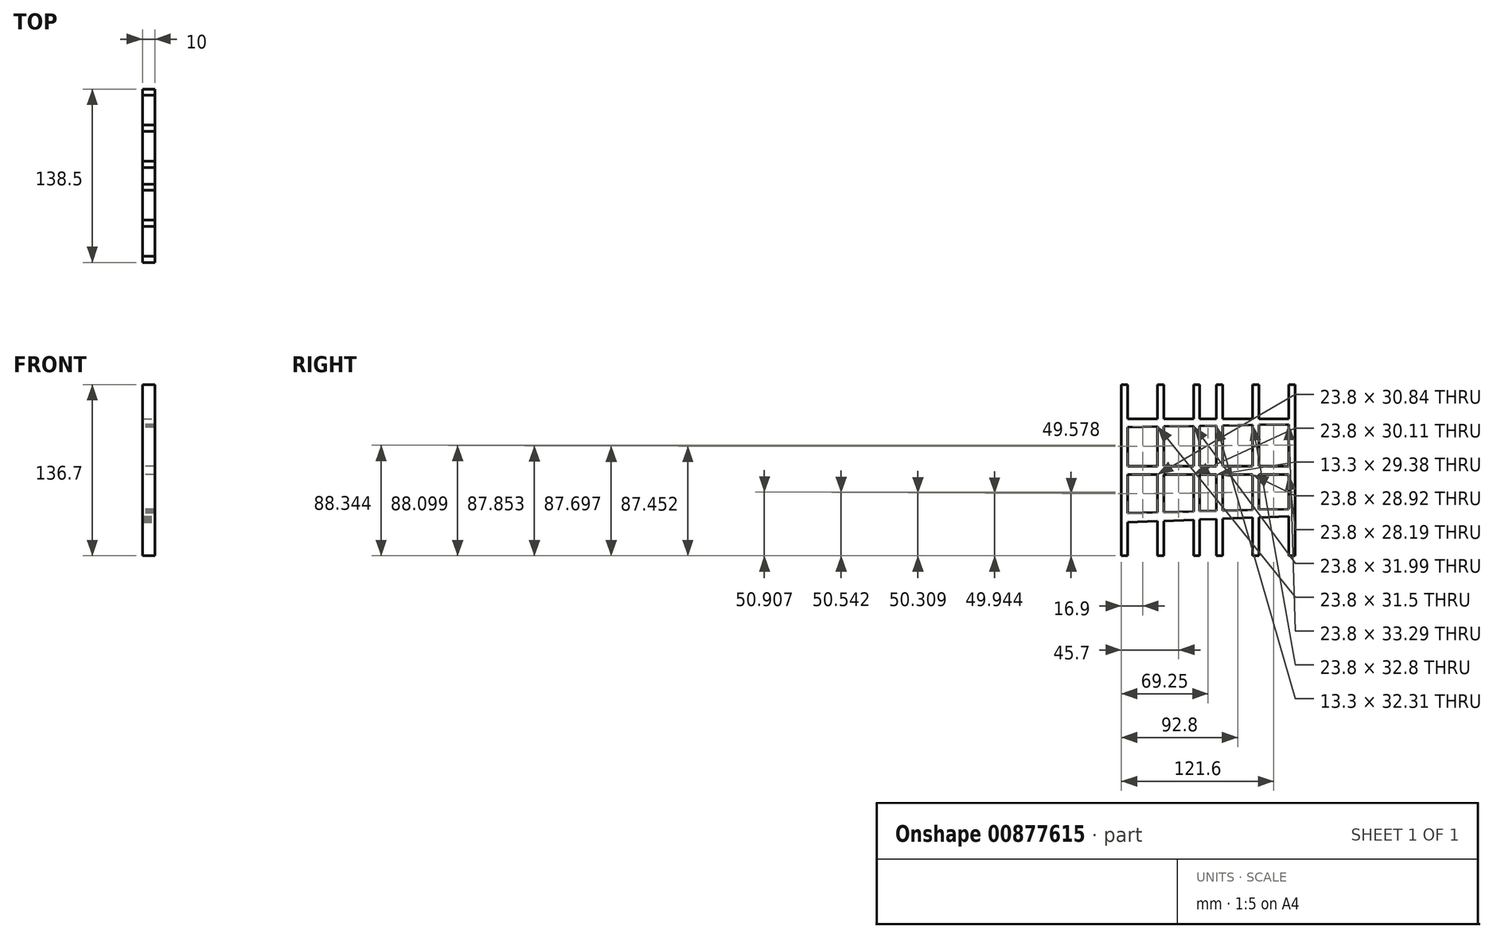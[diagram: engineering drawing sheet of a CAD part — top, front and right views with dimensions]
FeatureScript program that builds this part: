
annotation { "Feature Type Name" : "Feature", "Feature Type Description" : "" }
export const myFeature = defineFeature(function(context is Context, id is Id, definition is map)
    precondition{}
    {
        {
            var Q0;
            Q0=qCreatedBy(makeId("Right.planeOp"),FACE);
            var sketch = newSketch(context, id + "F0", { "sketchPlane" : qUnion([Q0])});
            skLineSegment(sketch, "E0", {"start": v(0, 0) * mm, "end": v(0, -65) * mm});
            skLineSegment(sketch, "E1", {"start": v(0, 0) * mm, "end": v(0, 65) * mm});
            skLineSegment(sketch, "E2", {"start": v(0, 0) * mm, "end": v(-5, 0) * mm});
            skLineSegment(sketch, "E3", {"start": v(-5, 0) * mm, "end": v(-5, 65) * mm});
            skLineSegment(sketch, "E4", {"start": v(-5, 65) * mm, "end": v(0, 65) * mm});
            skLineSegment(sketch, "E5", {"start": v(-5, 0) * mm, "end": v(-5, -65) * mm});
            skLineSegment(sketch, "E6", {"start": v(-5, -65) * mm, "end": v(0, -65) * mm});
            skLineSegment(sketch, "E7.0.1.0", {"start": v(-5, -6.7) * mm, "end": v(-5, 58.3) * mm});
            skLineSegment(sketch, "E7.0.1.1", {"start": v(0, -6.7) * mm, "end": v(0, -71.7) * mm});
            skLineSegment(sketch, "E7.0.1.2", {"start": v(0, -6.7) * mm, "end": v(0, 58.3) * mm});
            skLineSegment(sketch, "E7.0.1.3", {"start": v(-5, -6.7) * mm, "end": v(-5, -71.7) * mm});
            skLineSegment(sketch, "E7.0.1.4", {"start": v(-5, 58.3) * mm, "end": v(0, 58.3) * mm});
            skLineSegment(sketch, "E7.0.1.5", {"start": v(-5, -71.7) * mm, "end": v(0, -71.7) * mm});
            skLineSegment(sketch, "E7.0.1.6", {"start": v(0, -6.7) * mm, "end": v(-5, -6.7) * mm});
            skLineSegment(sketch, "E7.1.0.0", {"start": v(-33.8, 0) * mm, "end": v(-33.8, 65) * mm});
            skLineSegment(sketch, "E7.1.0.1", {"start": v(-28.8, 0) * mm, "end": v(-28.8, -65) * mm});
            skLineSegment(sketch, "E7.1.0.2", {"start": v(-28.8, 0) * mm, "end": v(-28.8, 65) * mm});
            skLineSegment(sketch, "E7.1.0.3", {"start": v(-33.8, 0) * mm, "end": v(-33.8, -65) * mm});
            skLineSegment(sketch, "E7.1.0.4", {"start": v(-33.8, 65) * mm, "end": v(-28.8, 65) * mm});
            skLineSegment(sketch, "E7.1.0.5", {"start": v(-33.8, -65) * mm, "end": v(-28.8, -65) * mm});
            skLineSegment(sketch, "E7.1.0.6", {"start": v(-28.8, 0) * mm, "end": v(-33.8, 0) * mm});
            skLineSegment(sketch, "E7.1.1.0", {"start": v(-33.8, -6.7) * mm, "end": v(-33.8, 58.3) * mm});
            skLineSegment(sketch, "E7.1.1.1", {"start": v(-28.8, -6.7) * mm, "end": v(-28.8, -71.7) * mm});
            skLineSegment(sketch, "E7.1.1.2", {"start": v(-28.8, -6.7) * mm, "end": v(-28.8, 58.3) * mm});
            skLineSegment(sketch, "E7.1.1.3", {"start": v(-33.8, -6.7) * mm, "end": v(-33.8, -71.7) * mm});
            skLineSegment(sketch, "E7.1.1.4", {"start": v(-33.8, 58.3) * mm, "end": v(-28.8, 58.3) * mm});
            skLineSegment(sketch, "E7.1.1.5", {"start": v(-33.8, -71.7) * mm, "end": v(-28.8, -71.7) * mm});
            skLineSegment(sketch, "E7.1.1.6", {"start": v(-28.8, -6.7) * mm, "end": v(-33.8, -6.7) * mm});
            skLineSegment(sketch, "E7.2.0.0", {"start": v(-62.6, 0) * mm, "end": v(-62.6, 65) * mm});
            skLineSegment(sketch, "E7.2.0.1", {"start": v(-57.6, 0) * mm, "end": v(-57.6, -65) * mm});
            skLineSegment(sketch, "E7.2.0.2", {"start": v(-57.6, 0) * mm, "end": v(-57.6, 65) * mm});
            skLineSegment(sketch, "E7.2.0.3", {"start": v(-62.6, 0) * mm, "end": v(-62.6, -65) * mm});
            skLineSegment(sketch, "E7.2.0.4", {"start": v(-62.6, 65) * mm, "end": v(-57.6, 65) * mm});
            skLineSegment(sketch, "E7.2.0.5", {"start": v(-62.6, -65) * mm, "end": v(-57.6, -65) * mm});
            skLineSegment(sketch, "E7.2.0.6", {"start": v(-57.6, 0) * mm, "end": v(-62.6, 0) * mm});
            skLineSegment(sketch, "E7.2.1.0", {"start": v(-62.6, -6.7) * mm, "end": v(-62.6, 58.3) * mm});
            skLineSegment(sketch, "E7.2.1.1", {"start": v(-57.6, -6.7) * mm, "end": v(-57.6, -71.7) * mm});
            skLineSegment(sketch, "E7.2.1.2", {"start": v(-57.6, -6.7) * mm, "end": v(-57.6, 58.3) * mm});
            skLineSegment(sketch, "E7.2.1.3", {"start": v(-62.6, -6.7) * mm, "end": v(-62.6, -71.7) * mm});
            skLineSegment(sketch, "E7.2.1.4", {"start": v(-62.6, 58.3) * mm, "end": v(-57.6, 58.3) * mm});
            skLineSegment(sketch, "E7.2.1.5", {"start": v(-62.6, -71.7) * mm, "end": v(-57.6, -71.7) * mm});
            skLineSegment(sketch, "E7.2.1.6", {"start": v(-57.6, -6.7) * mm, "end": v(-62.6, -6.7) * mm});
            skLineSegment(sketch, "E7.direction1", {"start": v(-5, -65) * mm, "end": v(-33.8, -65) * mm, "construction": true});
            skLineSegment(sketch, "E7.direction2", {"start": v(-5, -65) * mm, "end": v(-5, -71.7) * mm, "construction": true});
            skLineSegment(sketch, "E8.1.0.0", {"start": v(70.9, -65) * mm, "end": v(70.9, -71.7) * mm, "construction": true});
            skLineSegment(sketch, "E8.1.0.1", {"start": v(13.3, 0) * mm, "end": v(13.3, 65) * mm});
            skLineSegment(sketch, "E8.1.0.2", {"start": v(42.1, -6.7) * mm, "end": v(42.1, -71.7) * mm});
            skLineSegment(sketch, "E8.1.0.3", {"start": v(70.9, -65) * mm, "end": v(42.1, -65) * mm, "construction": true});
            skLineSegment(sketch, "E8.1.0.4", {"start": v(70.9, 0) * mm, "end": v(70.9, 65) * mm});
            skLineSegment(sketch, "E8.1.0.5", {"start": v(75.9, 0) * mm, "end": v(75.9, 65) * mm});
            skLineSegment(sketch, "E8.1.0.6", {"start": v(47.1, -6.7) * mm, "end": v(47.1, -71.7) * mm});
            skLineSegment(sketch, "E8.1.0.7", {"start": v(13.3, -6.7) * mm, "end": v(13.3, -71.7) * mm});
            skLineSegment(sketch, "E8.1.0.8", {"start": v(18.3, 0) * mm, "end": v(18.3, 65) * mm});
            skLineSegment(sketch, "E8.1.0.9", {"start": v(18.3, -6.7) * mm, "end": v(18.3, 58.3) * mm});
            skLineSegment(sketch, "E8.1.0.10", {"start": v(18.3, 0) * mm, "end": v(18.3, -65) * mm});
            skLineSegment(sketch, "E8.1.0.11", {"start": v(18.3, -6.7) * mm, "end": v(18.3, -71.7) * mm});
            skLineSegment(sketch, "E8.1.0.12", {"start": v(70.9, -6.7) * mm, "end": v(70.9, 58.3) * mm});
            skLineSegment(sketch, "E8.1.0.13", {"start": v(13.3, 0) * mm, "end": v(13.3, -65) * mm});
            skLineSegment(sketch, "E8.1.0.14", {"start": v(13.3, -6.7) * mm, "end": v(13.3, 58.3) * mm});
            skLineSegment(sketch, "E8.1.0.15", {"start": v(75.9, -6.7) * mm, "end": v(75.9, -71.7) * mm});
            skLineSegment(sketch, "E8.1.0.16", {"start": v(47.1, 0) * mm, "end": v(47.1, -65) * mm});
            skLineSegment(sketch, "E8.1.0.17", {"start": v(75.9, -6.7) * mm, "end": v(75.9, 58.3) * mm});
            skLineSegment(sketch, "E8.1.0.18", {"start": v(42.1, 0) * mm, "end": v(42.1, -65) * mm});
            skLineSegment(sketch, "E8.1.0.19", {"start": v(70.9, -6.7) * mm, "end": v(70.9, -71.7) * mm});
            skLineSegment(sketch, "E8.1.0.20", {"start": v(47.1, 0) * mm, "end": v(47.1, 65) * mm});
            skLineSegment(sketch, "E8.1.0.21", {"start": v(42.1, 0) * mm, "end": v(42.1, 65) * mm});
            skLineSegment(sketch, "E8.1.0.22", {"start": v(75.9, 0) * mm, "end": v(75.9, -65) * mm});
            skLineSegment(sketch, "E8.1.0.23", {"start": v(47.1, -6.7) * mm, "end": v(47.1, 58.3) * mm});
            skLineSegment(sketch, "E8.1.0.24", {"start": v(70.9, 0) * mm, "end": v(70.9, -65) * mm});
            skLineSegment(sketch, "E8.1.0.25", {"start": v(42.1, -6.7) * mm, "end": v(42.1, 58.3) * mm});
            skLineSegment(sketch, "E8.1.0.26", {"start": v(13.3, -71.7) * mm, "end": v(18.3, -71.7) * mm});
            skLineSegment(sketch, "E8.1.0.27", {"start": v(42.1, -71.7) * mm, "end": v(47.1, -71.7) * mm});
            skLineSegment(sketch, "E8.1.0.28", {"start": v(42.1, 58.3) * mm, "end": v(47.1, 58.3) * mm});
            skLineSegment(sketch, "E8.1.0.29", {"start": v(70.9, 65) * mm, "end": v(75.9, 65) * mm});
            skLineSegment(sketch, "E8.1.0.30", {"start": v(13.3, 58.3) * mm, "end": v(18.3, 58.3) * mm});
            skLineSegment(sketch, "E8.1.0.31", {"start": v(70.9, -65) * mm, "end": v(75.9, -65) * mm});
            skLineSegment(sketch, "E8.1.0.32", {"start": v(42.1, -65) * mm, "end": v(47.1, -65) * mm});
            skLineSegment(sketch, "E8.1.0.33", {"start": v(42.1, 65) * mm, "end": v(47.1, 65) * mm});
            skLineSegment(sketch, "E8.1.0.34", {"start": v(13.3, -65) * mm, "end": v(18.3, -65) * mm});
            skLineSegment(sketch, "E8.1.0.35", {"start": v(13.3, 65) * mm, "end": v(18.3, 65) * mm});
            skLineSegment(sketch, "E8.1.0.36", {"start": v(70.9, 58.3) * mm, "end": v(75.9, 58.3) * mm});
            skLineSegment(sketch, "E8.1.0.37", {"start": v(70.9, -71.7) * mm, "end": v(75.9, -71.7) * mm});
            skLineSegment(sketch, "E8.1.0.38", {"start": v(47.1, -6.7) * mm, "end": v(42.1, -6.7) * mm});
            skLineSegment(sketch, "E8.1.0.39", {"start": v(18.3, -6.7) * mm, "end": v(13.3, -6.7) * mm});
            skLineSegment(sketch, "E8.1.0.40", {"start": v(75.9, 0) * mm, "end": v(70.9, 0) * mm});
            skLineSegment(sketch, "E8.1.0.41", {"start": v(47.1, 0) * mm, "end": v(42.1, 0) * mm});
            skLineSegment(sketch, "E8.1.0.42", {"start": v(18.3, 0) * mm, "end": v(13.3, 0) * mm});
            skLineSegment(sketch, "E8.1.0.43", {"start": v(75.9, -6.7) * mm, "end": v(70.9, -6.7) * mm});
            skLineSegment(sketch, "E8.direction1", {"start": v(-62.6, -71.7) * mm, "end": v(13.3, -71.7) * mm, "construction": true});
            skLineSegment(sketch, "E9", {"start": v(75.9, 0) * mm, "end": v(-62.6, 0) * mm});
            skLineSegment(sketch, "E10", {"start": v(-62.6, -6.7) * mm, "end": v(75.9, -6.7) * mm});
            skSolve(sketch);
        }
        {
            var Q0;
            Q0 = qSketchRegion(id + "F0", true);
            extrude(context, id + "F1", {"entities" : qUnion([Q0]), "depth" : 10 * mm, "offsetDistance" : 25 * mm});
        }
        {
            var Q0;
            Q0=qCreatedBy(makeId("Right.planeOp"),FACE);
            var sketch = newSketch(context, id + "F2", { "sketchPlane" : qUnion([Q0])});
            skLineSegment(sketch, "E11", {"start": v(72.77, 37.6) * mm, "end": v(-59.16, 37.6) * mm});
            skLineSegment(sketch, "E12", {"start": v(-59.16, 37.6) * mm, "end": v(-59.16, 31.07) * mm});
            skLineSegment(sketch, "E13", {"start": v(-59.16, 31.07) * mm, "end": v(72.2, 33.31) * mm});
            skLineSegment(sketch, "E14", {"start": v(72.2, 33.31) * mm, "end": v(72.77, 37.6) * mm});
            skLineSegment(sketch, "E15", {"start": v(72.4, -34.24) * mm, "end": v(-59.91, -37.6) * mm});
            skLineSegment(sketch, "E16", {"start": v(-59.91, -37.6) * mm, "end": v(-59.72, -45.06) * mm});
            skLineSegment(sketch, "E17", {"start": v(-59.72, -45.06) * mm, "end": v(72.77, -40.03) * mm});
            skLineSegment(sketch, "E18", {"start": v(72.77, -40.03) * mm, "end": v(72.4, -34.24) * mm});
            skSolve(sketch);
        }
        {
            var Q0;
            Q0=makeQuery(id+"F2.imprint","IMPRINT",FACE,{"disambiguationData":[TD([[makeQuery(id+"F2.imprint","IMPRINT",EDGE,{"derivedFrom":sQuery(id+"F2.wireOp",EDGE,"E15")}),1.0]])]});
            var Q1;
            Q1=makeQuery(id+"F2.imprint","IMPRINT",FACE,{"disambiguationData":[TD([[makeQuery(id+"F2.imprint","IMPRINT",EDGE,{"derivedFrom":sQuery(id+"F2.wireOp",EDGE,"E11")}),1.0]])]});
            extrude(context, id + "F3", {"entities" : qUnion([Q0, Q1]), "operationType" : NewBodyOperationType.ADD, "depth" : 10 * mm, "offsetDistance" : 25 * mm});
        }
    });
